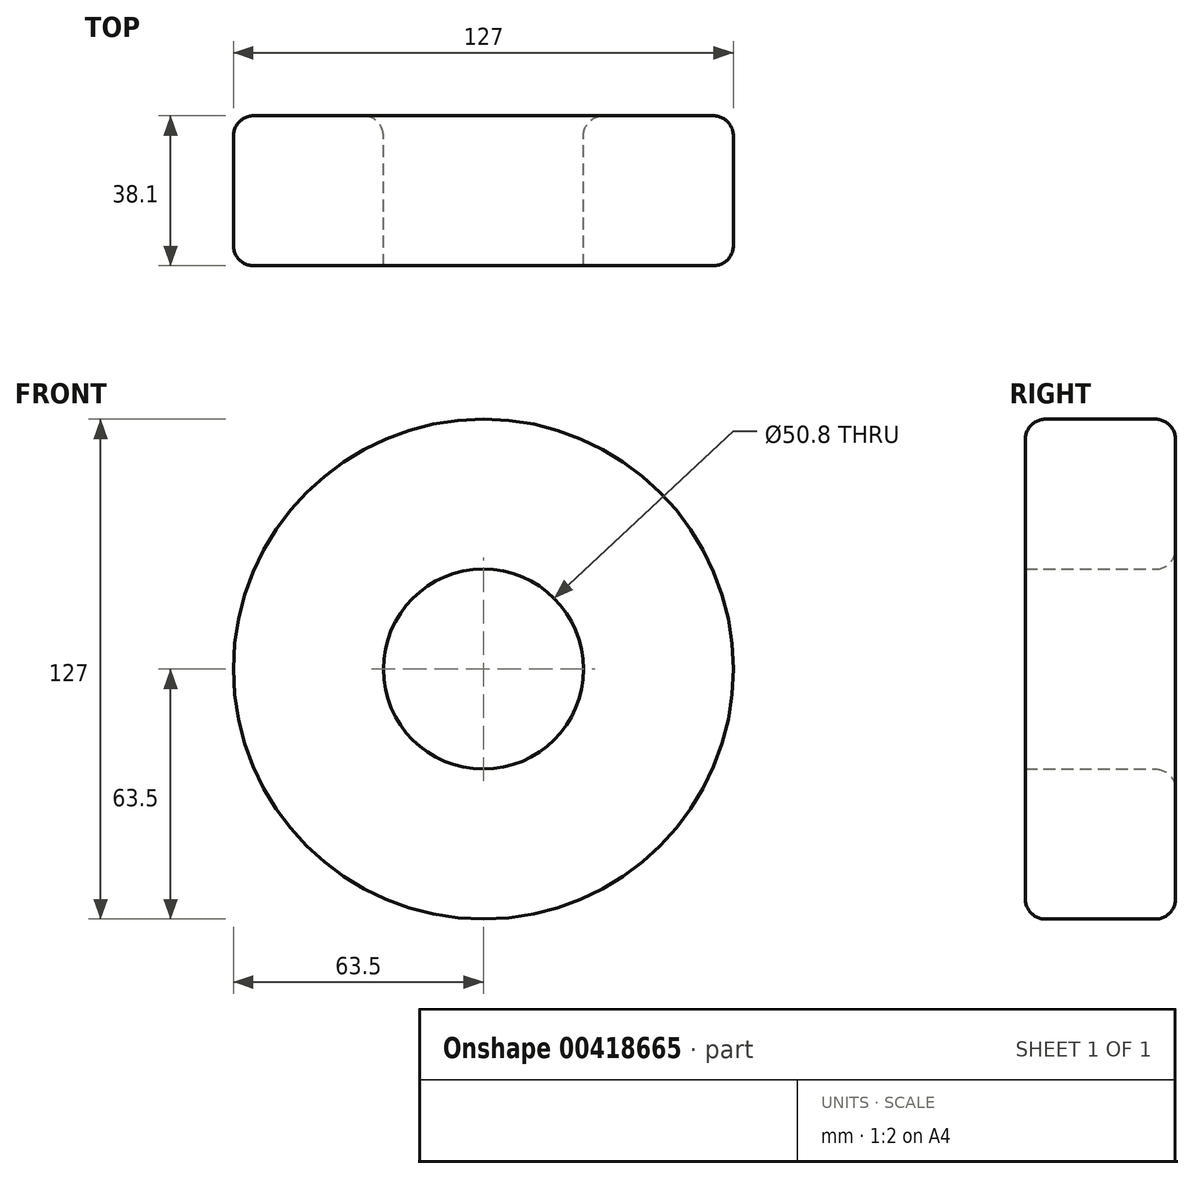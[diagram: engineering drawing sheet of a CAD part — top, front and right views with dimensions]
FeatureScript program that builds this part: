
annotation { "Feature Type Name" : "Feature", "Feature Type Description" : "" }
export const myFeature = defineFeature(function(context is Context, id is Id, definition is map)
    precondition{}
    {
        {
            var Q0;
            Q0=qCreatedBy(makeId("Front.planeOp"),FACE);
            var sketch = newSketch(context, id + "F0", { "sketchPlane" : qUnion([Q0])});
            skCircle(sketch, "E0", {"center": v(0, 0) * mm, "radius": 63.5 * mm});
            skCircle(sketch, "E1", {"center": v(0, 0) * mm, "radius": 25.4 * mm});
            skSolve(sketch);
        }
        {
            var Q0;
            Q0=makeQuery(id+"F0.imprint","IMPRINT",FACE,{"disambiguationData":[TD([[makeQuery(id+"F0.imprint","IMPRINT",EDGE,{"derivedFrom":sQuery(id+"F0.wireOp",EDGE,"E0")}),1.0]])]});
            extrude(context, id + "F1", {"entities" : qUnion([Q0]), "endBound" : BoundingType.SYMMETRIC, "depth" : 38.1 * mm});
        }
        {
            var Q0;
            Q0=makeQuery(id+"F1.opExtrude","CAP_EDGE",EDGE,{"disambiguationData":[OSD([sQuery(id+"F0.wireOp",EDGE,"E0")])],"isStart":false});
            var Q1;
            Q1=makeQuery(id+"F1.opExtrude","CAP_FACE",FACE,{"disambiguationData":[OSD([sQuery(id+"F0.wireOp",EDGE,"E0")])],"isStart":true});
            fillet(context, id + "F2", {"entities" : qUnion([Q0, Q1]), "radius" : 5.08 * mm, "tangentPropagation" : true, "allowEdgeOverflow" : false});
        }
    });
